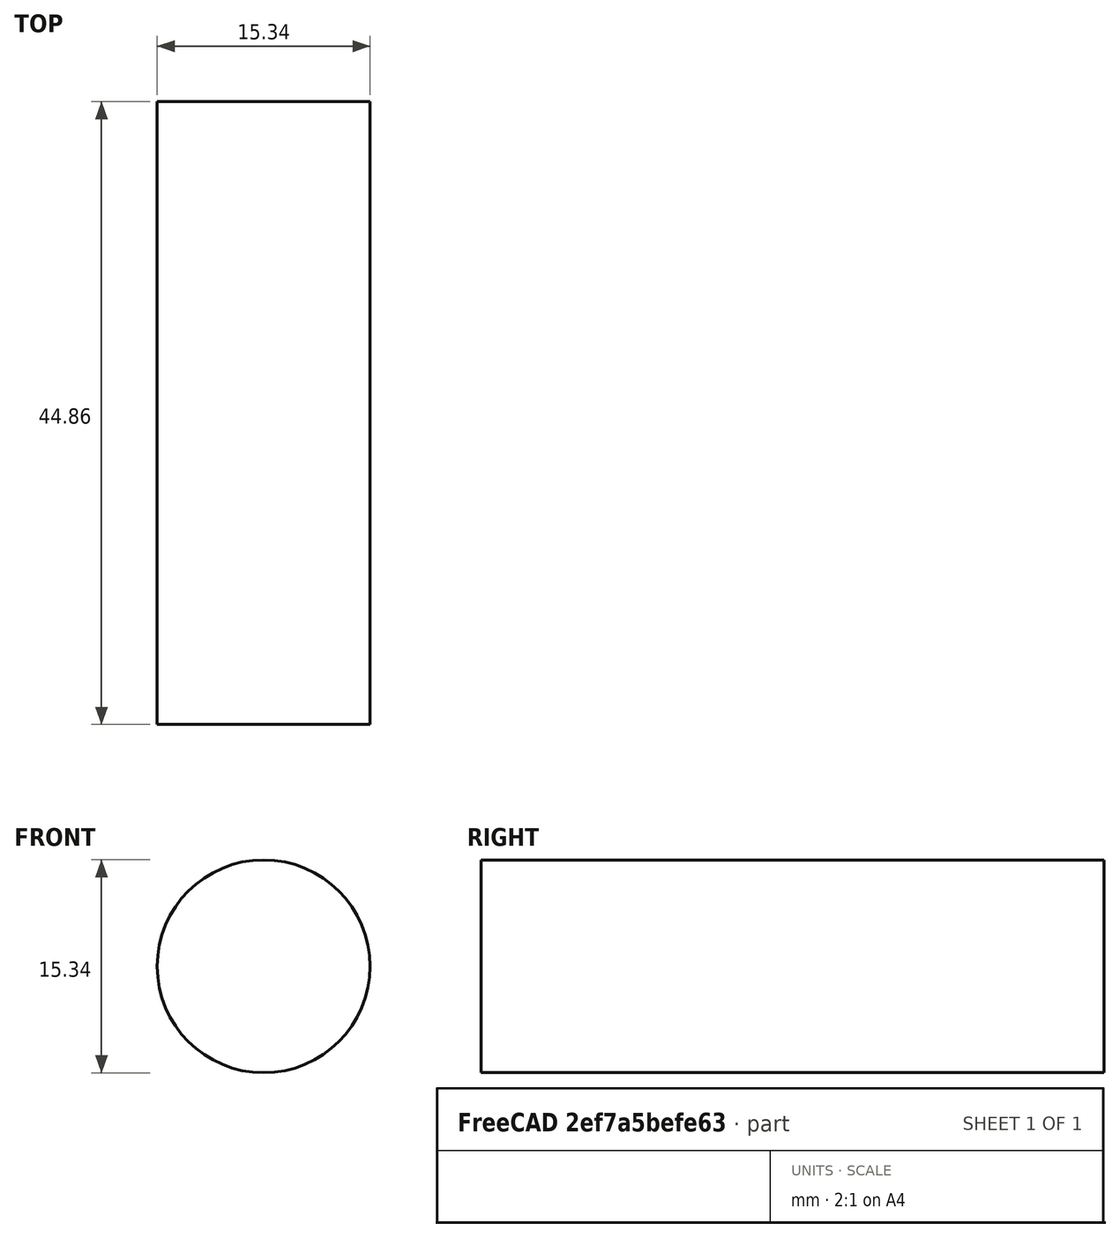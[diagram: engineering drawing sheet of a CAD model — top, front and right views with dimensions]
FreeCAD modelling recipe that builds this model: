
FCSTD DOCUMENT  (FreeCAD 0.20R29177 +426 (Git))
Label: Tornillo sin fin Corona A
License: All rights reserved
LicenseURL: http://en.wikipedia.org/wiki/All_rights_reserved
objects: Sketcher::SketchObject×2, PartDesign::Pad×1, PartDesign::Body×1
note: 5 computed .brp shape members not serialized (recipe doc carries the construction recipe); baked Part::Feature solids carry a one-line shape summary decoded from their .brp

FEATURE [Sketcher::SketchObject] Sketch
  FullyConstrained = true
  MapMode = 5
  Placement = pos=(0,0,0) rot=(1,0,0;1.5708rad)
  Support = -> [XZ_Plane]
  sketch-geometry (1):
    g0: Circle CenterX=0 CenterY=0 CenterZ=0 NormalX=0 NormalY=0 NormalZ=1 AngleXU=0 Radius=7.666
  constraints (2):
    c: Coincident(g0,g-1)
    c: Diameter(g0) = 15.332
FEATURE [PartDesign::Pad] Pad
  Direction = (0,-1,2e-16)
  Length = 44.862
  Length2 = 10
  Midplane = true
  Placement = pos=(0,0,0) rot=(1,0,0;1.5708rad)
  Profile = -> Sketch
  ReferenceAxis = -> Sketch [N_Axis]
  Type = 0
FEATURE [Sketcher::SketchObject] Sketch001
  FullyConstrained = false
  MapMode = 5
  Placement = pos=(0,0,0) rot=(0.57735,0.57735,0.57735;2.0944rad)
  Support = -> [YZ_Plane]
  sketch-geometry (9):
    g0: LineSegment StartX=-16.2044 StartY=12 StartZ=0 EndX=14.8752 EndY=12 EndZ=0
    g1: LineSegment StartX=-16.5658 StartY=10 StartZ=0 EndX=13.9115 EndY=10 EndZ=0
    g2: LineSegment StartX=-15.6021 StartY=7.6666 StartZ=0 EndX=13.9115 EndY=7.6666 EndZ=0
    g3: LineSegment StartX=-3.07652 StartY=7.6666 StartZ=0 EndX=-1.61705 EndY=12 EndZ=0
    g4: LineSegment StartX=-1.61705 StartY=12 StartZ=0 EndX=1.66317 EndY=12 EndZ=0
    g5: LineSegment StartX=1.66317 StartY=12 StartZ=0 EndX=2.97023 EndY=7.6666 EndZ=0
    g6: LineSegment StartX=2.97023 StartY=7.6666 StartZ=0 EndX=2.97023 EndY=6.37472 EndZ=0
    g7: LineSegment StartX=2.97023 StartY=6.37472 StartZ=0 EndX=-3.07652 EndY=6.37472 EndZ=0
    g8: LineSegment StartX=-3.07652 StartY=6.37472 StartZ=0 EndX=-3.07652 EndY=7.6666 EndZ=0
  constraints (19):
    c: Horizontal(g0)
    c: Horizontal(g1)
    c: Horizontal(g2)
    c: DistanceY(g-1,g2) = 7.6666
    c: DistanceY(g-1,g1) = 10
    c: DistanceY(g-1,g0) = 12
    c: PointOnObject(g3,g2)
    c: PointOnObject(g3,g0)
    c: Coincident(g3,g4)
    c: PointOnObject(g4,g0)
    c: Coincident(g4,g5)
    c: PointOnObject(g5,g2)
    c: Coincident(g5,g6)
    c: Vertical(g6)
    c: Coincident(g6,g7)
    c: Horizontal(g7)
    c: Coincident(g7,g8)
    c: Coincident(g8,g3)
    c: Vertical(g8)
FEATURE [PartDesign::Body] Body
  Group = -> [Sketch,Pad,Sketch001]
  Origin = -> Origin
  Tip = -> Pad
